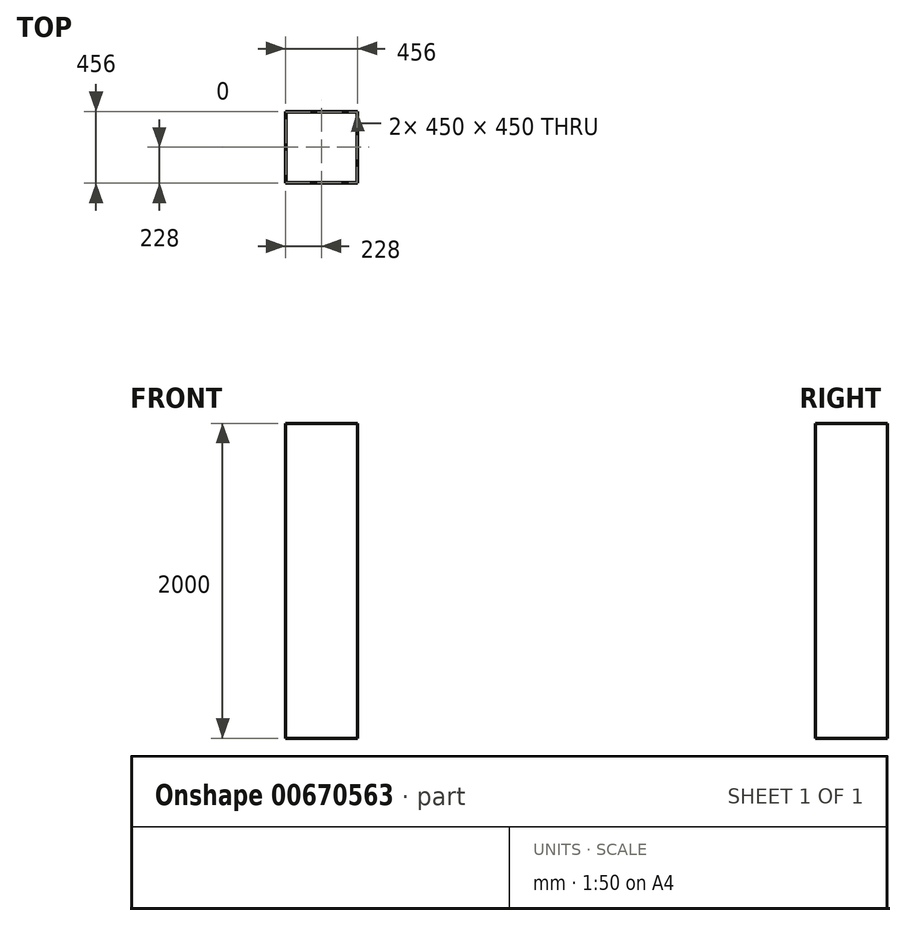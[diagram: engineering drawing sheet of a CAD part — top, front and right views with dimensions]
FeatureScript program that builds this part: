
annotation { "Feature Type Name" : "Feature", "Feature Type Description" : "" }
export const myFeature = defineFeature(function(context is Context, id is Id, definition is map)
    precondition{}
    {
        {
            var Q0;
            Q0=qCreatedBy(makeId("Top.planeOp"),FACE);
            var sketch = newSketch(context, id + "F0", { "sketchPlane" : qUnion([Q0])});
            skLineSegment(sketch, "E0.bottom", {"start": v(225, -225) * mm, "end": v(-225, -225) * mm});
            skLineSegment(sketch, "E0.top", {"start": v(225, 225) * mm, "end": v(-225, 225) * mm});
            skLineSegment(sketch, "E0.left", {"start": v(225, -225) * mm, "end": v(225, 225) * mm});
            skLineSegment(sketch, "E0.right", {"start": v(-225, -225) * mm, "end": v(-225, 225) * mm});
            skPoint(sketch, "E0.middle", {"position": v(0, 0) * mm});
            skLineSegment(sketch, "E1.0", {"start": v(228, 228) * mm, "end": v(-228, 228) * mm});
            skLineSegment(sketch, "E1.1", {"start": v(228, -228) * mm, "end": v(228, 228) * mm});
            skLineSegment(sketch, "E1.2", {"start": v(228, -228) * mm, "end": v(-228, -228) * mm});
            skLineSegment(sketch, "E1.3", {"start": v(-228, -228) * mm, "end": v(-228, 228) * mm});
            skLineSegment(sketch, "E2", {"start": v(-228, 0) * mm, "end": v(228, 0) * mm, "construction": true});
            skLineSegment(sketch, "E3", {"start": v(0, -228) * mm, "end": v(0, 228) * mm, "construction": true});
            skSolve(sketch);
        }
        {
            var Q0;
            Q0=makeQuery(id+"F0.imprint","IMPRINT",FACE,{"disambiguationData":[TD([[makeQuery(id+"F0.imprint","IMPRINT",EDGE,{"derivedFrom":sQuery(id+"F0.wireOp",EDGE,"E0.bottom")}),1.0]])]});
            extrude(context, id + "F1", {"entities" : qUnion([Q0]), "depth" : 2000 * mm, "offsetDistance" : 25 * mm});
        }
    });
